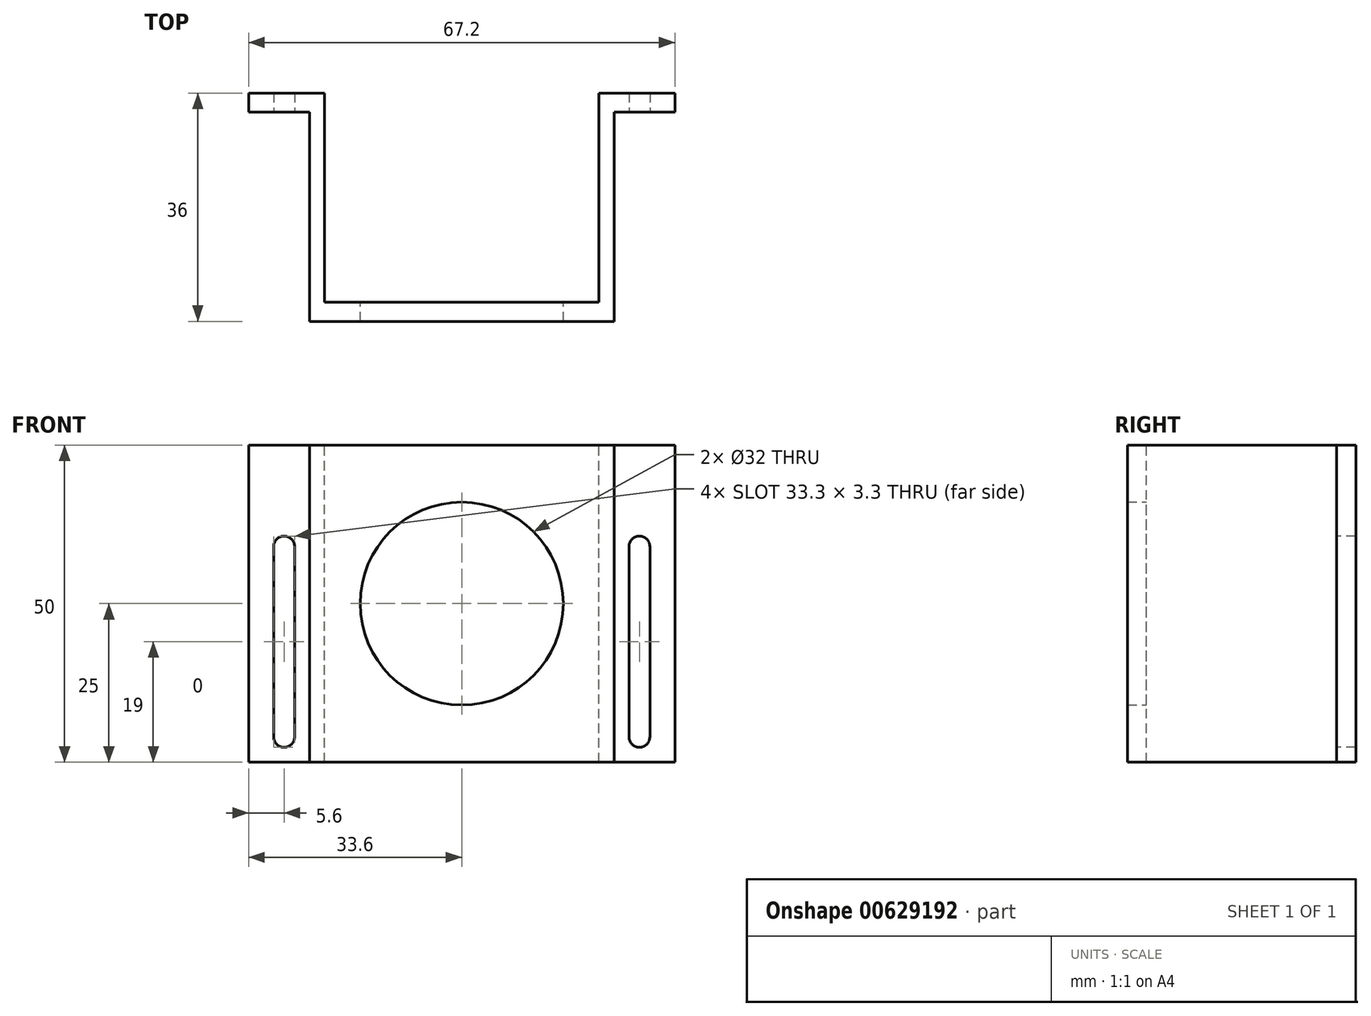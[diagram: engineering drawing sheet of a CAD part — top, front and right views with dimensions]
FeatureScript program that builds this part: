
annotation { "Feature Type Name" : "Feature", "Feature Type Description" : "" }
export const myFeature = defineFeature(function(context is Context, id is Id, definition is map)
    precondition{}
    {
        {
            var Q0;
            Q0=qCreatedBy(makeId("Front.planeOp"),FACE);
            var sketch = newSketch(context, id + "F0", { "sketchPlane" : qUnion([Q0])});
            skLineSegment(sketch, "E0.bottom", {"start": v(24, -25) * mm, "end": v(-24, -25) * mm});
            skLineSegment(sketch, "E0.top", {"start": v(24, 25) * mm, "end": v(-24, 25) * mm});
            skLineSegment(sketch, "E0.left", {"start": v(24, -25) * mm, "end": v(24, 25) * mm});
            skLineSegment(sketch, "E0.right", {"start": v(-24, -25) * mm, "end": v(-24, 25) * mm});
            skPoint(sketch, "E0.middle", {"position": v(0, 0) * mm});
            skCircle(sketch, "E1", {"center": v(0, 0) * mm, "radius": 16 * mm});
            skSolve(sketch);
        }
        {
            var Q0;
            Q0=makeQuery(id+"F0.imprint","IMPRINT",FACE,{"disambiguationData":[TD([[makeQuery(id+"F0.imprint","IMPRINT",EDGE,{"derivedFrom":sQuery(id+"F0.wireOp",EDGE,"E0.bottom")}),-1.0]])]});
            extrude(context, id + "F1", {"entities" : qUnion([Q0]), "depth" : 3 * mm, "offsetDistance" : 25 * mm});
        }
        {
            var Q0;
            Q0=makeQuery(id+"F1.opExtrude","CAP_FACE",FACE,{"disambiguationData":[OSD([sQuery(id+"F0.wireOp",EDGE,"E0.bottom"),sQuery(id+"F0.wireOp",EDGE,"E0.top"),sQuery(id+"F0.wireOp",EDGE,"E0.left"),sQuery(id+"F0.wireOp",EDGE,"E0.right"),sQuery(id+"F0.wireOp",EDGE,"E1")])],"isStart":true});
            var sketch = newSketch(context, id + "F2", { "sketchPlane" : qUnion([Q0])});
            skLineSegment(sketch, "E2.bottom", {"start": v(24, -25) * mm, "end": v(21.6, -25) * mm});
            skLineSegment(sketch, "E2.top", {"start": v(24, 25) * mm, "end": v(21.6, 25) * mm});
            skLineSegment(sketch, "E2.left", {"start": v(24, -25) * mm, "end": v(24, 25) * mm});
            skLineSegment(sketch, "E2.right", {"start": v(21.6, -25) * mm, "end": v(21.6, 25) * mm});
            skLineSegment(sketch, "E3.MirrorCS", {"start": v(-24, -25) * mm, "end": v(-21.6, -25) * mm});
            skLineSegment(sketch, "E4.MirrorCS", {"start": v(-24, 25) * mm, "end": v(-21.6, 25) * mm});
            skLineSegment(sketch, "E5.MirrorCS", {"start": v(-24, -25) * mm, "end": v(-24, 25) * mm});
            skLineSegment(sketch, "E6.MirrorCS", {"start": v(-21.6, -25) * mm, "end": v(-21.6, 25) * mm});
            skSolve(sketch);
        }
        {
            var Q0;
            Q0=makeQuery(id+"F2.imprint","IMPRINT",FACE,{"disambiguationData":[TD([[makeQuery(id+"F2.imprint","IMPRINT",EDGE,{"derivedFrom":sQuery(id+"F2.wireOp",EDGE,"E3.MirrorCS")}),1.0]])]});
            var Q1;
            Q1=makeQuery(id+"F2.imprint","IMPRINT",FACE,{"disambiguationData":[TD([[makeQuery(id+"F2.imprint","IMPRINT",EDGE,{"derivedFrom":sQuery(id+"F2.wireOp",EDGE,"E2.bottom")}),1.0]])]});
            extrude(context, id + "F3", {"entities" : qUnion([Q0, Q1]), "operationType" : NewBodyOperationType.ADD, "depth" : 30 * mm, "offsetDistance" : 25 * mm});
        }
        {
            var Q0;
            Q0=makeQuery(id+"F3.opExtrude","CAP_FACE",FACE,{"disambiguationData":[OSD([sQuery(id+"F2.wireOp",EDGE,"E3.MirrorCS"),sQuery(id+"F2.wireOp",EDGE,"E4.MirrorCS"),sQuery(id+"F2.wireOp",EDGE,"E5.MirrorCS"),sQuery(id+"F2.wireOp",EDGE,"E6.MirrorCS")])],"isStart":false});
            var sketch = newSketch(context, id + "F4", { "sketchPlane" : qUnion([Q0])});
            skLineSegment(sketch, "E7.bottom", {"start": v(-21.6, 25) * mm, "end": v(-33.6, 25) * mm});
            skLineSegment(sketch, "E7.top", {"start": v(-21.6, -25) * mm, "end": v(-33.6, -25) * mm});
            skLineSegment(sketch, "E7.left", {"start": v(-21.6, 25) * mm, "end": v(-21.6, -25) * mm});
            skLineSegment(sketch, "E7.right", {"start": v(-33.6, 25) * mm, "end": v(-33.6, -25) * mm});
            skLineSegment(sketch, "E8.MirrorCS", {"start": v(33.6, 25) * mm, "end": v(33.6, -25) * mm});
            skLineSegment(sketch, "E9.MirrorCS", {"start": v(21.6, 25) * mm, "end": v(21.6, -25) * mm});
            skLineSegment(sketch, "E10.MirrorCS", {"start": v(21.6, 25) * mm, "end": v(33.6, 25) * mm});
            skLineSegment(sketch, "E11.MirrorCS", {"start": v(21.6, -25) * mm, "end": v(33.6, -25) * mm});
            skLineSegment(sketch, "E12.left", {"start": v(-29.65, 9) * mm, "end": v(-29.65, -21) * mm});
            skLineSegment(sketch, "E12.right", {"start": v(-26.35, 9) * mm, "end": v(-26.35, -21) * mm});
            skArc(sketch, "E13", {"start": v(-29.65, -21) * mm, "mid": v(-28, -22.65) * mm, "end": v(-26.35, -21) * mm});
            skArc(sketch, "E14", {"start": v(-26.35, 9) * mm, "mid": v(-28, 10.65) * mm, "end": v(-29.65, 9) * mm});
            skLineSegment(sketch, "E15.MirrorCS", {"start": v(26.35, 9) * mm, "end": v(26.35, -21) * mm});
            skArc(sketch, "E16.MirrorCS", {"start": v(29.65, -21) * mm, "mid": v(28, -22.65) * mm, "end": v(26.35, -21) * mm});
            skLineSegment(sketch, "E17.MirrorCS", {"start": v(29.65, 9) * mm, "end": v(29.65, -21) * mm});
            skArc(sketch, "E18.MirrorCS", {"start": v(26.35, 9) * mm, "mid": v(28, 10.65) * mm, "end": v(29.65, 9) * mm});
            skSolve(sketch);
        }
        {
            var Q0;
            Q0 = qSketchRegion(id + "F4", true);
            extrude(context, id + "F5", {"entities" : qUnion([Q0]), "operationType" : NewBodyOperationType.ADD, "depth" : 3 * mm, "offsetDistance" : 25 * mm});
        }
        {
            var Q0;
            Q0=makeQuery(id+"F1.opExtrude","SWEPT_BODY",BODY,{"disambiguationData":[OSD([sQuery(id+"F0.wireOp",EDGE,"E0.bottom"),sQuery(id+"F0.wireOp",EDGE,"E0.top"),sQuery(id+"F0.wireOp",EDGE,"E0.left"),sQuery(id+"F0.wireOp",EDGE,"E0.right"),sQuery(id+"F0.wireOp",EDGE,"E1")])]});
            transform(context, id + "F6", {"entities" : qUnion([Q0]), "transformType" : TransformType.TRANSLATION_3D, "dx" : 0 * mm, "dy" : 0 * mm, "dz" : 0 * mm, "makeCopy" : true});
        }
    });
